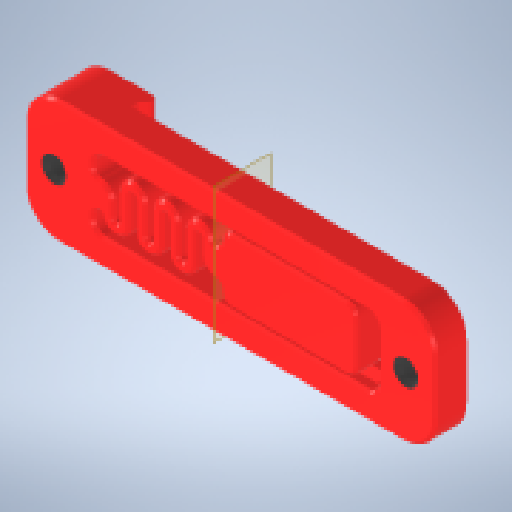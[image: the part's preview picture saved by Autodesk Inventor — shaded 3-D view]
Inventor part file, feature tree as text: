
AUTODESK INVENTOR PART (.ipt)
format: ipt  version: 2023.1 (Build 271208000, 208)  size: 488,448 bytes
history: native  units: mm
features: move_body x3, direct_edit x2, fillet x2, chamfer x2, sketch x2, extrude x1, hole x1, plane x1
ambient origin geometry x8: Origin, YZ Plane, XZ Plane, XY Plane, X Axis, Y Axis, Z Axis, Center Point
bodies: Volumenkörper2 (feature_tree), Body3 (feature_tree)
feature tree (14):
  direct_edit  "Direktbearbeitung1"
  extrude  "Extrusion1"  Depth=1.0mm
  fillet  "Rundung1"  Radius=1.0mm
  chamfer  "Fase1"  Distance=10.0mm
  fillet  "Rundung2"  Radius=0.8mm
  hole  "Bohrung1"  [1 undecoded]
  chamfer  "Fase2"  Distance=0.4mm
  direct_edit  "Direktbearbeitung2"
  plane  "Arbeitsebene2"
  sketch  "Skizze1"  dims[d0=0.0mm d1=0.0mm d2=1.5mm d3=1.0mm d4=1.0mm d6=10.0mm d7=0.0mm d8=0.8mm]
  sketch  "Skizze2"  dims[d9=0.5mm d10=2.0mm d11=45.0deg d12=0.8mm d13=2.86mm d14=6.0mm d15=5.8mm d16=3.0mm d17=90.0deg d18=8.0mm d19=20.594885mm d20=0.4mm d21=2.0mm d22=11.34464mm d23=0.0mm d24=0.0mm d25=3.0mm d26=1.5mm d27=0.0mm d28=0.0mm]
  move_body  "Verschieben1"
  move_body  "Verschieben2"
  move_body  "Verschieben3"
note: 1 required parameter value undecoded (feature->parameter linkage not recoverable at this tier; creation-order binding heuristic only, values carry confidence <= 0.55)
